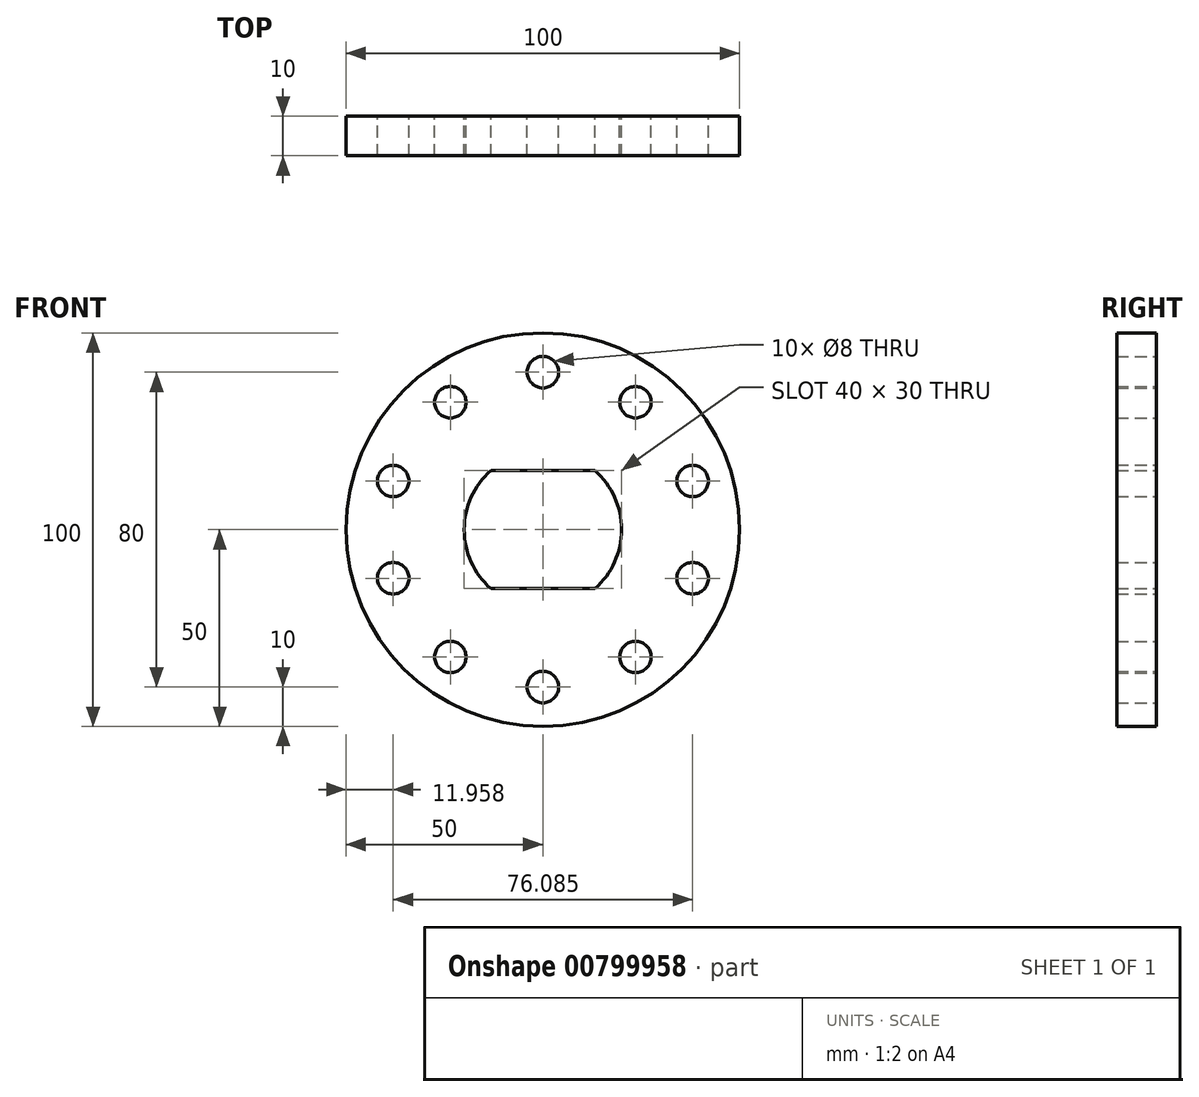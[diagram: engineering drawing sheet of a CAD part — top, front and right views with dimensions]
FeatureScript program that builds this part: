
annotation { "Feature Type Name" : "Feature", "Feature Type Description" : "" }
export const myFeature = defineFeature(function(context is Context, id is Id, definition is map)
    precondition{}
    {
        {
            var Q0;
            Q0=qCreatedBy(makeId("Front.planeOp"),FACE);
            var sketch = newSketch(context, id + "F0", { "sketchPlane" : qUnion([Q0])});
            skArc(sketch, "E0", {"start": v(-13.23, 15) * mm, "mid": v(-20, 0) * mm, "end": v(-13.23, -15) * mm});
            skArc(sketch, "E1", {"start": v(-4, 39.8) * mm, "mid": v(0, -40) * mm, "end": v(4, 39.8) * mm});
            skCircle(sketch, "E2", {"center": v(0, 0) * mm, "radius": 50 * mm});
            skLineSegment(sketch, "E3.bottom", {"start": v(-13.23, 15) * mm, "end": v(13.23, 15) * mm});
            skLineSegment(sketch, "E3.top", {"start": v(-13.23, -15) * mm, "end": v(13.23, -15) * mm});
            skArc(sketch, "E4.trimOffspring", {"start": v(13.23, -15) * mm, "mid": v(20, 0) * mm, "end": v(13.23, 15) * mm});
            skCircle(sketch, "E5", {"center": v(0, 0) * mm, "radius": 25 * mm});
            skCircle(sketch, "E6", {"center": v(0, 40) * mm, "radius": 4 * mm});
            skCircle(sketch, "E7.1.0", {"center": v(-23.51, 32.36) * mm, "radius": 4 * mm});
            skCircle(sketch, "E7.2.0", {"center": v(-38.04, 12.36) * mm, "radius": 4 * mm});
            skCircle(sketch, "E7.3.0", {"center": v(-38.04, -12.36) * mm, "radius": 4 * mm});
            skCircle(sketch, "E7.4.0", {"center": v(-23.51, -32.36) * mm, "radius": 4 * mm});
            skCircle(sketch, "E7.5.0", {"center": v(0, -40) * mm, "radius": 4 * mm});
            skCircle(sketch, "E7.6.0", {"center": v(23.51, -32.36) * mm, "radius": 4 * mm});
            skCircle(sketch, "E7.7.0", {"center": v(38.04, -12.36) * mm, "radius": 4 * mm});
            skCircle(sketch, "E7.8.0", {"center": v(38.04, 12.36) * mm, "radius": 4 * mm});
            skCircle(sketch, "E7.9.0", {"center": v(23.51, 32.36) * mm, "radius": 4 * mm});
            skSolve(sketch);
        }
        {
            var Q0;
            Q0=makeQuery(id+"F0.imprint","IMPRINT",FACE,{"disambiguationData":[TD([[makeQuery(id+"F0.imprint","IMPRINT",EDGE,{"derivedFrom":sQuery(id+"F0.wireOp",EDGE,"E5")}),-1.0]])]});
            var Q1;
            Q1=makeQuery(id+"F0.imprint","IMPRINT",FACE,{"disambiguationData":[TD([[makeQuery(id+"F0.imprint","IMPRINT",EDGE,{"derivedFrom":sQuery(id+"F0.wireOp",EDGE,"E2")}),1.0]])]});
            var Q2;
            Q2=makeQuery(id+"F0.imprint","IMPRINT",FACE,{"disambiguationData":[TD([[makeQuery(id+"F0.imprint","IMPRINT",EDGE,{"derivedFrom":sQuery(id+"F0.wireOp",EDGE,"E0")}),-1.0]])]});
            extrude(context, id + "F1", {"entities" : qUnion([Q0, Q1, Q2]), "depth" : 10 * mm, "offsetDistance" : 25 * mm});
        }
    });
